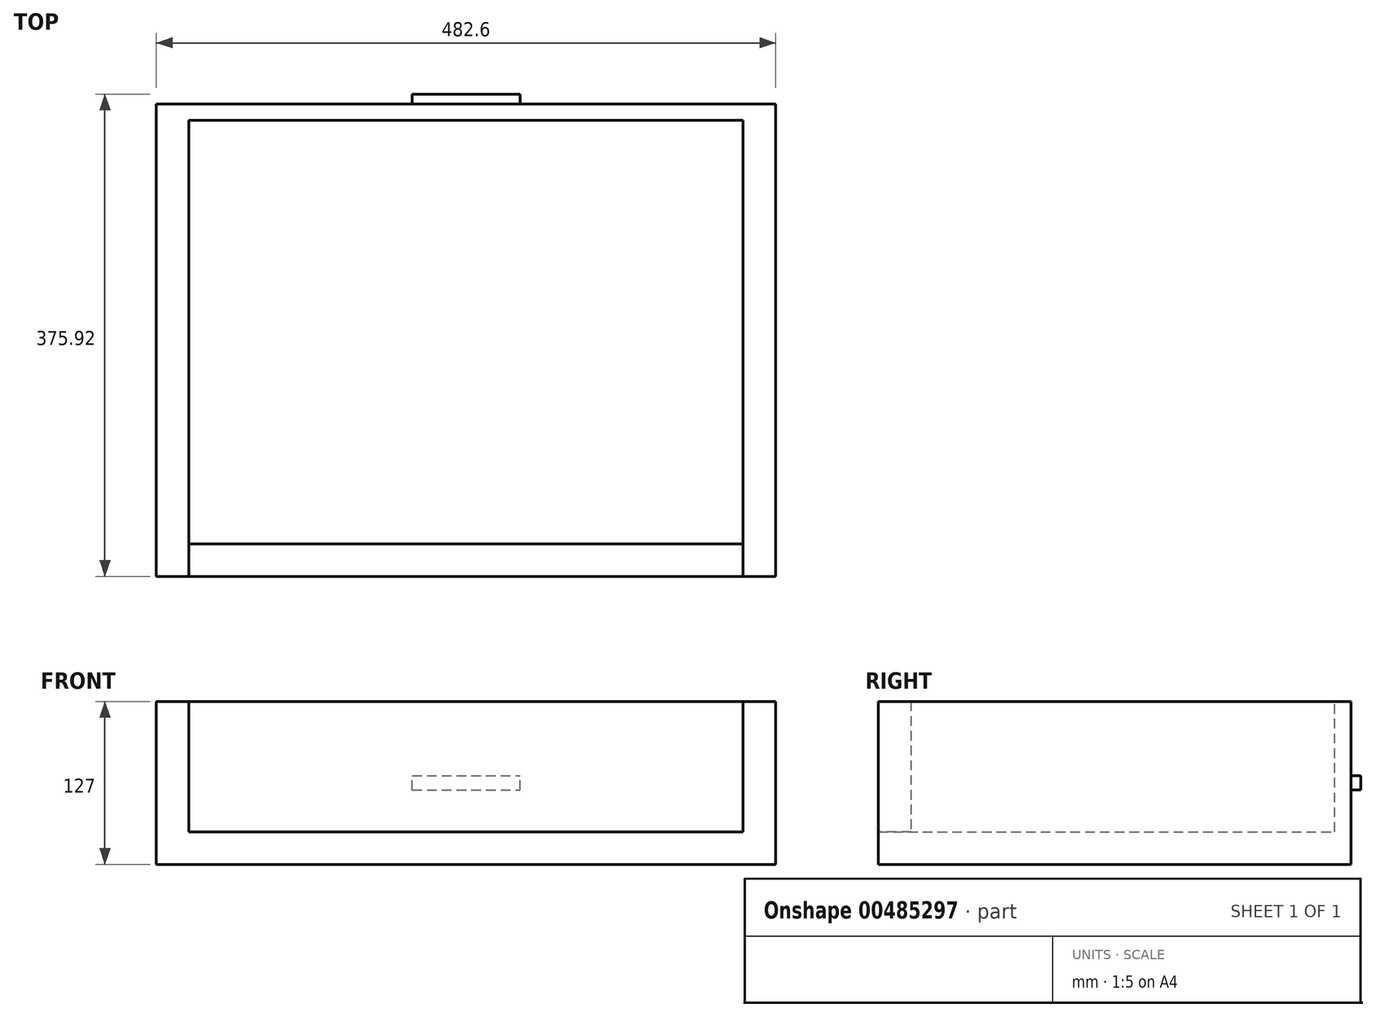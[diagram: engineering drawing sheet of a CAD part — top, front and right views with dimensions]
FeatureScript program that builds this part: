
annotation { "Feature Type Name" : "Feature", "Feature Type Description" : "" }
export const myFeature = defineFeature(function(context is Context, id is Id, definition is map)
    precondition{}
    {
        {
            var Q0;
            Q0=qCreatedBy(makeId("Front.planeOp"),FACE);
            var sketch = newSketch(context, id + "F0", { "sketchPlane" : qUnion([Q0])});
            skLineSegment(sketch, "E0.bottom", {"start": v(241.3, -63.5) * mm, "end": v(-241.3, -63.5) * mm});
            skLineSegment(sketch, "E0.top", {"start": v(241.3, 63.5) * mm, "end": v(215.9, 63.5) * mm});
            skLineSegment(sketch, "E0.left", {"start": v(241.3, -63.5) * mm, "end": v(241.3, 63.5) * mm});
            skLineSegment(sketch, "E0.right", {"start": v(-241.3, -63.5) * mm, "end": v(-241.3, 63.5) * mm});
            skPoint(sketch, "E0.middle", {"position": v(0, 0) * mm});
            skLineSegment(sketch, "E1", {"start": v(-215.9, 63.5) * mm, "end": v(-215.9, -38.1) * mm});
            skLineSegment(sketch, "E2", {"start": v(-215.9, -38.1) * mm, "end": v(215.9, -38.1) * mm});
            skLineSegment(sketch, "E3", {"start": v(215.9, -38.1) * mm, "end": v(215.9, 63.5) * mm});
            skLineSegment(sketch, "E4.trimOffspring", {"start": v(-215.9, 63.5) * mm, "end": v(-241.3, 63.5) * mm});
            skSolve(sketch);
        }
        {
            var Q0;
            Q0=makeQuery(id+"F0.imprint","IMPRINT",FACE,{"disambiguationData":[TD([[makeQuery(id+"F0.imprint","IMPRINT",EDGE,{"derivedFrom":sQuery(id+"F0.wireOp",EDGE,"E0.bottom")}),-1.0]])]});
            extrude(context, id + "F1", {"entities" : qUnion([Q0]), "depth" : 355.6 * mm});
        }
        {
            var Q0;
            Q0=makeQuery(id+"F1.opExtrude","CAP_FACE",FACE,{"disambiguationData":[OSD([sQuery(id+"F0.wireOp",EDGE,"E0.bottom"),sQuery(id+"F0.wireOp",EDGE,"E0.top"),sQuery(id+"F0.wireOp",EDGE,"E0.left"),sQuery(id+"F0.wireOp",EDGE,"E0.right"),sQuery(id+"F0.wireOp",EDGE,"E1"),sQuery(id+"F0.wireOp",EDGE,"E2"),sQuery(id+"F0.wireOp",EDGE,"E3"),sQuery(id+"F0.wireOp",EDGE,"E4.trimOffspring")])],"isStart":false});
            var sketch = newSketch(context, id + "F2", { "sketchPlane" : qUnion([Q0])});
            skLineSegment(sketch, "E5.0", {"start": v(241.3, -63.5) * mm, "end": v(-241.3, -63.5) * mm});
            skLineSegment(sketch, "E6.0", {"start": v(-241.3, -63.5) * mm, "end": v(-241.3, 63.5) * mm});
            skLineSegment(sketch, "E7.0", {"start": v(241.3, -63.5) * mm, "end": v(241.3, 63.5) * mm});
            skLineSegment(sketch, "E8", {"start": v(-241.3, 63.5) * mm, "end": v(241.3, 63.5) * mm});
            skSolve(sketch);
        }
        {
            var Q0;
            {var subQ2=makeQuery(id+"F1.opExtrude","CAP_EDGE",EDGE,{"disambiguationData":[OSD([sQuery(id+"F0.wireOp",EDGE,"E1")])],"isStart":false});Q0=makeQuery(id+"F2.imprint","IMPRINT",FACE,{"disambiguationData":[TD([[makeQuery(id+"F2.imprint","IMPRINT",EDGE,{"derivedFrom":subQ2}),1.0]])]});}
            extrude(context, id + "F3", {"entities" : qUnion([Q0]), "oppositeDirection" : true, "depth" : 25.4 * mm});
        }
        {
            var Q0;
            Q0=makeQuery(id+"F1.opExtrude","CAP_FACE",FACE,{"disambiguationData":[OSD([sQuery(id+"F0.wireOp",EDGE,"E0.bottom"),sQuery(id+"F0.wireOp",EDGE,"E0.top"),sQuery(id+"F0.wireOp",EDGE,"E0.left"),sQuery(id+"F0.wireOp",EDGE,"E0.right"),sQuery(id+"F0.wireOp",EDGE,"E1"),sQuery(id+"F0.wireOp",EDGE,"E2"),sQuery(id+"F0.wireOp",EDGE,"E3"),sQuery(id+"F0.wireOp",EDGE,"E4.trimOffspring")])],"isStart":true});
            var sketch = newSketch(context, id + "F4", { "sketchPlane" : qUnion([Q0])});
            skPoint(sketch, "E9.0", {"position": v(-241.3, 63.5) * mm});
            skPoint(sketch, "E10.0", {"position": v(-241.3, -63.5) * mm});
            skPoint(sketch, "E11.0", {"position": v(241.3, 63.5) * mm});
            skPoint(sketch, "E12.0", {"position": v(241.3, -63.5) * mm});
            skLineSegment(sketch, "E13", {"start": v(-241.3, 63.5) * mm, "end": v(-241.3, -63.5) * mm});
            skLineSegment(sketch, "E14", {"start": v(241.3, -63.5) * mm, "end": v(241.3, 63.5) * mm});
            skLineSegment(sketch, "E15", {"start": v(-241.3, 63.5) * mm, "end": v(241.3, 63.5) * mm});
            skLineSegment(sketch, "E16", {"start": v(-241.3, -63.5) * mm, "end": v(241.3, -63.5) * mm});
            skSolve(sketch);
        }
        {
            var Q0;
            Q0 = qSketchRegion(id + "F4", true);
            extrude(context, id + "F5", {"entities" : qUnion([Q0]), "operationType" : NewBodyOperationType.ADD, "depth" : 12.7 * mm});
        }
        {
            var Q0;
            Q0=makeQuery(id+"F5.opExtrude","CAP_FACE",FACE,{"disambiguationData":[OSD([sQuery(id+"F4.wireOp",EDGE,"E13"),sQuery(id+"F4.wireOp",EDGE,"E14"),sQuery(id+"F4.wireOp",EDGE,"E15"),sQuery(id+"F4.wireOp",EDGE,"E16")])],"isStart":false});
            var sketch = newSketch(context, id + "F6", { "sketchPlane" : qUnion([Q0])});
            skLineSegment(sketch, "E17.bottom", {"start": v(41.96, -5.53) * mm, "end": v(-41.96, -5.53) * mm});
            skLineSegment(sketch, "E17.top", {"start": v(41.96, 5.53) * mm, "end": v(-41.96, 5.53) * mm});
            skLineSegment(sketch, "E17.left", {"start": v(41.96, -5.53) * mm, "end": v(41.96, 5.53) * mm});
            skLineSegment(sketch, "E17.right", {"start": v(-41.96, -5.53) * mm, "end": v(-41.96, 5.53) * mm});
            skPoint(sketch, "E17.middle", {"position": v(0, 0) * mm});
            skSolve(sketch);
        }
        {
            var Q0;
            Q0=makeQuery(id+"F6.imprint","IMPRINT",FACE,{"disambiguationData":[TD([[makeQuery(id+"F6.imprint","IMPRINT",EDGE,{"derivedFrom":sQuery(id+"F6.wireOp",EDGE,"E17.bottom")}),-1.0]])]});
            extrude(context, id + "F7", {"entities" : qUnion([Q0]), "operationType" : NewBodyOperationType.ADD, "depth" : 7.62 * mm});
        }
    });
